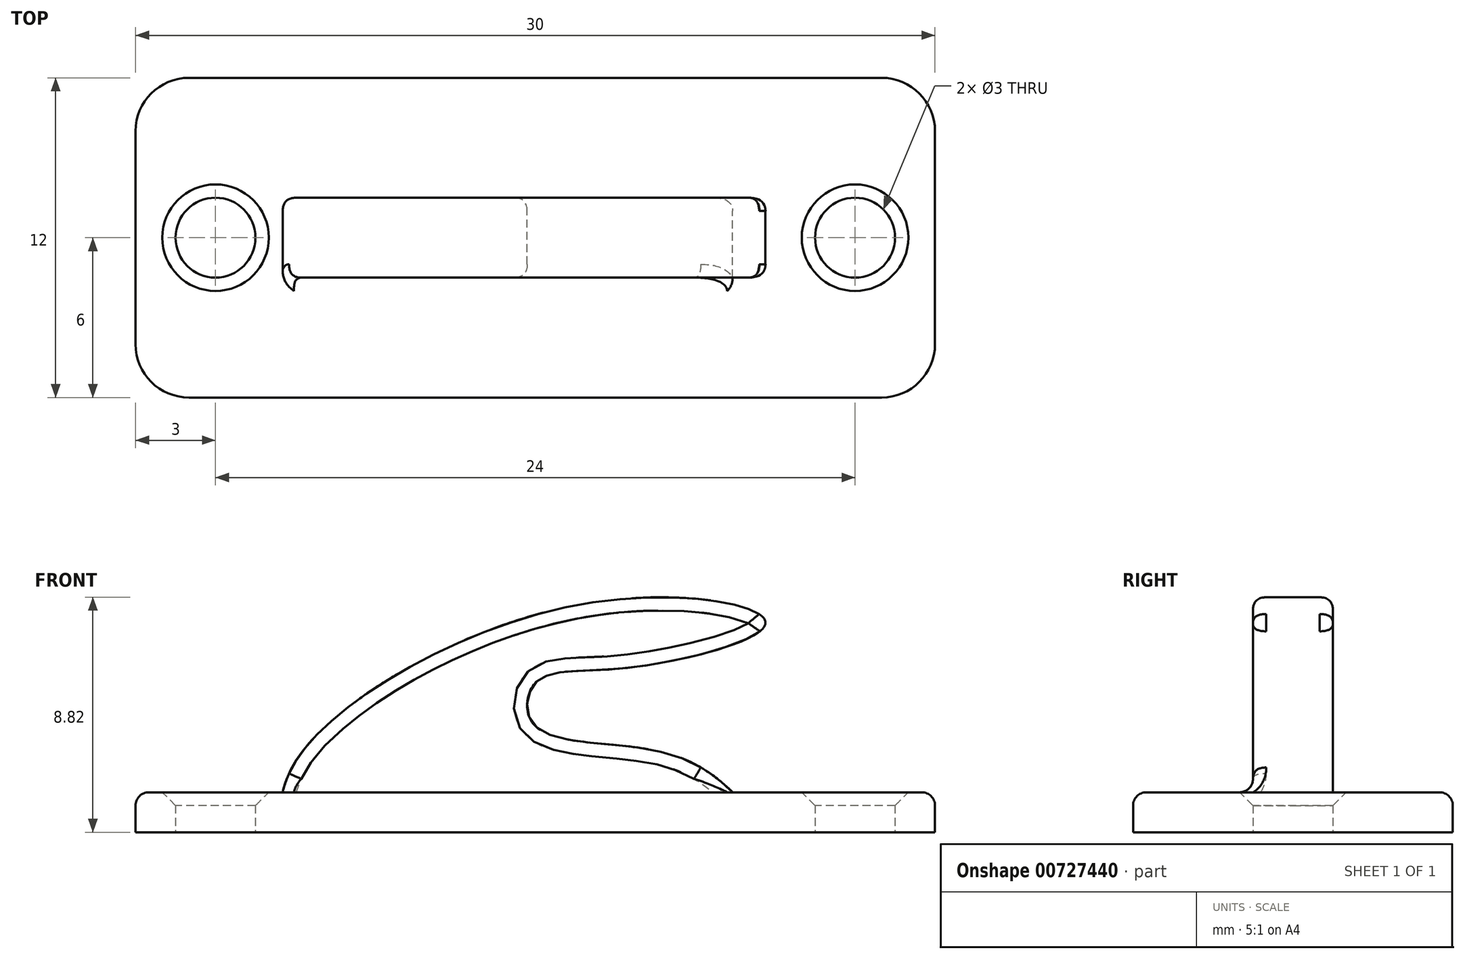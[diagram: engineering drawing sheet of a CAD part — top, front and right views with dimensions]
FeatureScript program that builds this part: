
annotation { "Feature Type Name" : "Feature", "Feature Type Description" : "" }
export const myFeature = defineFeature(function(context is Context, id is Id, definition is map)
    precondition{}
    {
        {
            var Q0;
            Q0=qCreatedBy(makeId("Top.planeOp"),FACE);
            var sketch = newSketch(context, id + "F0", { "sketchPlane" : qUnion([Q0])});
            skLineSegment(sketch, "E0", {"start": v(-51.46, 0) * mm, "end": v(51.66, 0) * mm, "construction": true});
            skLineSegment(sketch, "E1", {"start": v(0, 36.35) * mm, "end": v(0, -33.08) * mm, "construction": true});
            skLineSegment(sketch, "E2.0", {"start": v(-51.46, -6) * mm, "end": v(51.66, -6) * mm, "construction": true});
            skLineSegment(sketch, "E3.0", {"start": v(-51.46, 6) * mm, "end": v(51.66, 6) * mm, "construction": true});
            skLineSegment(sketch, "E4.0", {"start": v(-15, 36.35) * mm, "end": v(-15, -33.08) * mm, "construction": true});
            skLineSegment(sketch, "E5.0", {"start": v(15, 36.35) * mm, "end": v(15, -33.08) * mm, "construction": true});
            skLineSegment(sketch, "E6.bottom", {"start": v(-15, 6) * mm, "end": v(15, 6) * mm});
            skLineSegment(sketch, "E6.top", {"start": v(-15, -6) * mm, "end": v(15, -6) * mm});
            skLineSegment(sketch, "E6.left", {"start": v(-15, 6) * mm, "end": v(-15, -6) * mm});
            skLineSegment(sketch, "E6.right", {"start": v(15, 6) * mm, "end": v(15, -6) * mm});
            skLineSegment(sketch, "E7.0", {"start": v(-12, 36.35) * mm, "end": v(-12, -33.08) * mm, "construction": true});
            skCircle(sketch, "E8", {"center": v(-12, 0) * mm, "radius": 1.5 * mm});
            skCircle(sketch, "E9.MirrorC", {"center": v(12, 0) * mm, "radius": 1.5 * mm});
            skSolve(sketch);
        }
        {
            var Q0;
            Q0=makeQuery(id+"F0.imprint","IMPRINT",FACE,{"disambiguationData":[TD([[makeQuery(id+"F0.imprint","IMPRINT",EDGE,{"derivedFrom":sQuery(id+"F0.wireOp",EDGE,"E6.bottom")}),-1.0]])]});
            extrude(context, id + "F1", {"entities" : qUnion([Q0]), "depth" : 1.5 * mm, "offsetDistance" : 25 * mm});
        }
        {
            var Q0;
            Q0=makeQuery(id+"F1.opExtrude","SWEPT_EDGE",EDGE,{"disambiguationData":[OSD([sQuery(id+"F0.wireOp",EDGE,"E6.bottom"),sQuery(id+"F0.wireOp",EDGE,"E6.left")])]});
            var Q1;
            Q1=makeQuery(id+"F1.opExtrude","SWEPT_EDGE",EDGE,{"disambiguationData":[OSD([sQuery(id+"F0.wireOp",EDGE,"E6.top"),sQuery(id+"F0.wireOp",EDGE,"E6.left")])]});
            var Q2;
            Q2=makeQuery(id+"F1.opExtrude","SWEPT_EDGE",EDGE,{"disambiguationData":[OSD([sQuery(id+"F0.wireOp",EDGE,"E6.bottom"),sQuery(id+"F0.wireOp",EDGE,"E6.right")])]});
            var Q3;
            Q3=makeQuery(id+"F1.opExtrude","SWEPT_EDGE",EDGE,{"disambiguationData":[OSD([sQuery(id+"F0.wireOp",EDGE,"E6.top"),sQuery(id+"F0.wireOp",EDGE,"E6.right")])]});
            fillet(context, id + "F2", {"entities" : qUnion([Q0, Q1, Q2, Q3]), "radius" : 2 * mm, "tangentPropagation" : true, "allowEdgeOverflow" : false});
        }
        {
            var Q0;
            Q0=makeQuery(id+"F1.opExtrude","CAP_EDGE",EDGE,{"disambiguationData":[OSD([sQuery(id+"F0.wireOp",EDGE,"E6.top")])],"isStart":false});
            fillet(context, id + "F3", {"entities" : qUnion([Q0]), "radius" : .5 * mm, "tangentPropagation" : true, "allowEdgeOverflow" : false});
        }
        {
            var Q0;
            Q0=makeQuery(id+"F1.opExtrude","CAP_EDGE",EDGE,{"disambiguationData":[OSD([sQuery(id+"F0.wireOp",EDGE,"E8")])],"isStart":false});
            var Q1;
            Q1=makeQuery(id+"F1.opExtrude","CAP_EDGE",EDGE,{"disambiguationData":[OSD([sQuery(id+"F0.wireOp",EDGE,"E9.MirrorC")])],"isStart":false});
            chamfer(context, id + "F4", {"entities" : qUnion([Q0, Q1]), "width" : .5 * mm, "tangentPropagation" : true});
        }
        {
            var Q0;
            Q0=qCreatedBy(makeId("Front.planeOp"),FACE);
            var sketch = newSketch(context, id + "F5", { "sketchPlane" : qUnion([Q0])});
            skFitSpline(sketch, "E10", {"points": [v(-9.6, 0) * mm, v(-8.81, 2.93) * mm, v(2.14, 8.63) * mm, v(8.64, 7.81) * mm, v(3.14, 6.14) * mm, v(0, 5.6) * mm, v(0, 3.98) * mm, v(5.07, 2.93) * mm, v(8.73, 0) * mm], "startDerivative": vector(0.01, 28.23) * mm, "endDerivative": vector(24.39, -29.84) * mm});
            skLineSegment(sketch, "E11", {"start": v(-9.6, 0) * mm, "end": v(8.73, 0) * mm});
            skSolve(sketch);
        }
        {
            var Q0;
            Q0 = qSketchRegion(id + "F5", true);
            extrude(context, id + "F6", {"entities" : qUnion([Q0]), "operationType" : NewBodyOperationType.ADD, "depth" : 1.5 * mm, "offsetDistance" : 25 * mm});
        }
        {
            var Q0;
            Q0=makeQuery(id+"F6.opExtrude","CAP_FACE",FACE,{"disambiguationData":[OSD([sQuery(id+"F5.wireOp",EDGE,"E10"),sQuery(id+"F5.wireOp",EDGE,"E11")])],"isStart":true});
            extrude(context, id + "F7", {"entities" : qUnion([Q0]), "operationType" : NewBodyOperationType.ADD, "depth" : 1.5 * mm, "offsetDistance" : 25 * mm});
        }
        {
            var Q0;
            Q0=makeQuery(id+"F6.boolean.opBoolean","INTERSECT",EDGE,{"derivedFrom":[makeQuery(id+"F1.opExtrude","CAP_FACE",FACE,{"disambiguationData":[OSD([sQuery(id+"F0.wireOp",EDGE,"E6.bottom"),sQuery(id+"F0.wireOp",EDGE,"E6.top"),sQuery(id+"F0.wireOp",EDGE,"E6.left"),sQuery(id+"F0.wireOp",EDGE,"E6.right"),sQuery(id+"F0.wireOp",EDGE,"E8"),sQuery(id+"F0.wireOp",EDGE,"E9.MirrorC")])],"isStart":false}),makeQuery(id+"F6.opExtrude","CAP_FACE",FACE,{"disambiguationData":[OSD([sQuery(id+"F5.wireOp",EDGE,"E10"),sQuery(id+"F5.wireOp",EDGE,"E11")])],"isStart":false})]});
            var Q1;
            Q1=makeQuery(id+"F7.opExtrude","CAP_EDGE",EDGE,{"disambiguationData":[OSD([sQuery(id+"F0.wireOp",EDGE,"E6.bottom"),sQuery(id+"F0.wireOp",EDGE,"E6.top"),sQuery(id+"F0.wireOp",EDGE,"E6.left"),sQuery(id+"F0.wireOp",EDGE,"E6.right"),sQuery(id+"F0.wireOp",EDGE,"E8"),sQuery(id+"F0.wireOp",EDGE,"E9.MirrorC"),sQuery(id+"F5.wireOp",EDGE,"E10"),sQuery(id+"F5.wireOp",EDGE,"E11")])],"isStart":false});
            fillet(context, id + "F8", {"entities" : qUnion([Q0, Q1]), "radius" : .5 * mm, "tangentPropagation" : true, "allowEdgeOverflow" : false});
        }
        {
            var Q0;
            Q0=makeQuery(id+"F6.opExtrude","CAP_EDGE",EDGE,{"disambiguationData":[OSD([sQuery(id+"F5.wireOp",EDGE,"E10")])],"isStart":false});
            var Q1;
            Q1=makeQuery(id+"F7.opExtrude","CAP_EDGE",EDGE,{"disambiguationData":[OSD([sQuery(id+"F5.wireOp",EDGE,"E10")])],"isStart":false});
            fillet(context, id + "F9", {"entities" : qUnion([Q0, Q1]), "radius" : .5 * mm, "tangentPropagation" : true, "rho" : 0.5, "crossSection" : FilletCrossSection.CONIC, "allowEdgeOverflow" : false});
        }
    });
